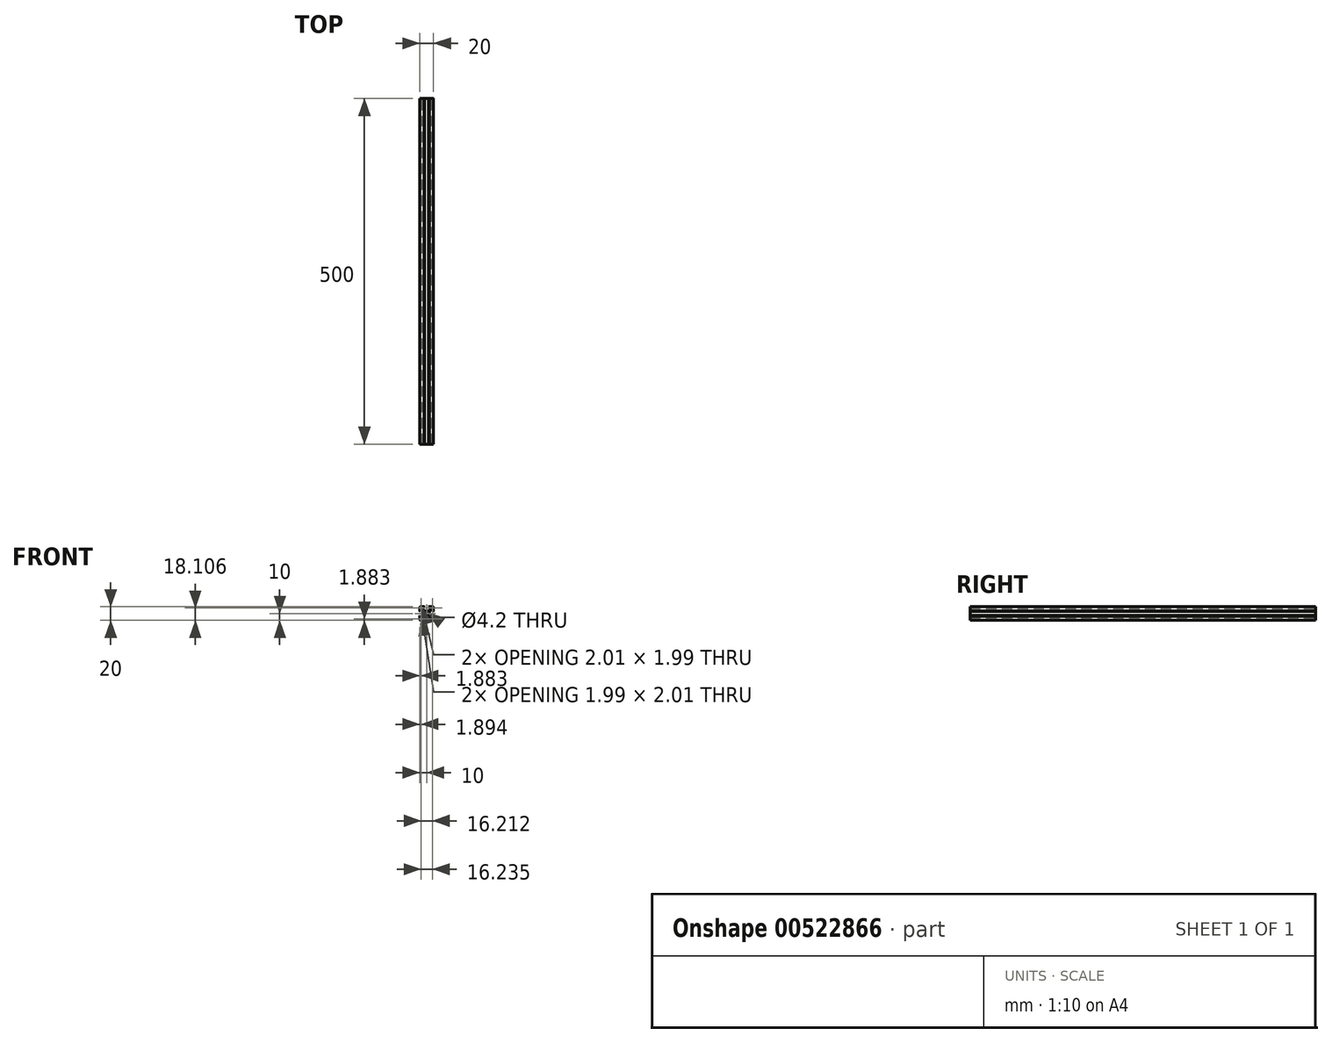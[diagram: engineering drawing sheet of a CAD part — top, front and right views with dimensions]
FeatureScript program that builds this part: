
annotation { "Feature Type Name" : "Feature", "Feature Type Description" : "" }
export const myFeature = defineFeature(function(context is Context, id is Id, definition is map)
    precondition{}
    {
        {
            var Q0;
            Q0=qCreatedBy(makeId("Front.planeOp"),FACE);
            var sketch = newSketch(context, id + "F0", { "sketchPlane" : qUnion([Q0])});
            skCircle(sketch, "E0", {"center": v(0, 0) * mm, "radius": 2.1 * mm});
            skLineSegment(sketch, "E1.bottom", {"start": v(-10, 10) * mm, "end": v(10, 10) * mm});
            skLineSegment(sketch, "E1.top", {"start": v(-10, -10) * mm, "end": v(10, -10) * mm});
            skLineSegment(sketch, "E1.left", {"start": v(-10, 10) * mm, "end": v(-10, -10) * mm});
            skLineSegment(sketch, "E1.right", {"start": v(10, 10) * mm, "end": v(10, -10) * mm});
            skLineSegment(sketch, "E2.bottom", {"start": v(-9.1, 9.1) * mm, "end": v(6.4, 9.1) * mm});
            skLineSegment(sketch, "E2.top", {"start": v(-9.1, -9.1) * mm, "end": v(9.1, -9.1) * mm});
            skLineSegment(sketch, "E2.left", {"start": v(-9.1, 9.1) * mm, "end": v(-9.1, -9.1) * mm});
            skLineSegment(sketch, "E2.right", {"start": v(9.1, 6.4) * mm, "end": v(9.1, -9.1) * mm});
            skLineSegment(sketch, "E3", {"start": v(-7.93, 7.93) * mm, "end": v(-1.48, 1.48) * mm});
            skLineSegment(sketch, "E4.0", {"start": v(7.46, 6.4) * mm, "end": v(1.92, 0.86) * mm});
            skLineSegment(sketch, "E5.MirrorCS", {"start": v(6.4, 7.46) * mm, "end": v(0.86, 1.92) * mm});
            skLineSegment(sketch, "E6.0", {"start": v(-8.47, 7.41) * mm, "end": v(-1.92, 0.86) * mm});
            skLineSegment(sketch, "E7.MirrorCS", {"start": v(-7.4, 8.46) * mm, "end": v(-0.86, 1.92) * mm});
            skPoint(sketch, "E8.orphan", {"position": v(-9.63, 8.57) * mm});
            skPoint(sketch, "E9.orphan", {"position": v(-8.57, 9.63) * mm});
            skPoint(sketch, "E10.orphan", {"position": v(8.05, 9.11) * mm});
            skPoint(sketch, "E11.orphan", {"position": v(9.11, 8.05) * mm});
            skPoint(sketch, "E12.orphan", {"position": v(9.63, -8.57) * mm});
            skPoint(sketch, "E13.orphan", {"position": v(8.57, -9.63) * mm});
            skPoint(sketch, "E14.orphan", {"position": v(-9.09, -10.15) * mm});
            skPoint(sketch, "E15.orphan", {"position": v(-10.15, -9.09) * mm});
            skLineSegment(sketch, "E16.trimOffspring", {"start": v(1.92, -0.86) * mm, "end": v(8.47, -7.41) * mm});
            skLineSegment(sketch, "E17.trimOffspring", {"start": v(0.86, -1.92) * mm, "end": v(7.4, -8.46) * mm});
            skLineSegment(sketch, "E18.trimOffspring", {"start": v(1.48, -1.48) * mm, "end": v(7.93, -7.93) * mm});
            skLineSegment(sketch, "E19.trimOffspring", {"start": v(-0.86, -1.92) * mm, "end": v(-7.41, -8.47) * mm});
            skLineSegment(sketch, "E20.trimOffspring", {"start": v(-1.48, -1.48) * mm, "end": v(-7.93, -7.93) * mm});
            skLineSegment(sketch, "E21.trimOffspring", {"start": v(-1.92, -0.86) * mm, "end": v(-8.46, -7.4) * mm});
            skLineSegment(sketch, "E22", {"start": v(-3.9, -2.84) * mm, "end": v(-3.9, 2.84) * mm});
            skLineSegment(sketch, "E23.1.0", {"start": v(2.84, -3.9) * mm, "end": v(-2.84, -3.9) * mm});
            skLineSegment(sketch, "E23.2.0", {"start": v(3.9, 2.84) * mm, "end": v(3.9, -2.84) * mm});
            skLineSegment(sketch, "E23.3.0", {"start": v(-2.84, 3.9) * mm, "end": v(2.84, 3.9) * mm});
            skLineSegment(sketch, "E24", {"start": v(-9.1, 2.84) * mm, "end": v(-9.1, -2.84) * mm});
            skLineSegment(sketch, "E25.1.0", {"start": v(-2.84, -9.1) * mm, "end": v(2.84, -9.1) * mm});
            skLineSegment(sketch, "E25.2.0", {"start": v(9.1, -2.84) * mm, "end": v(9.1, 2.84) * mm});
            skLineSegment(sketch, "E25.3.0", {"start": v(2.84, 9.1) * mm, "end": v(-2.84, 9.1) * mm});
            skLineSegment(sketch, "E26", {"start": v(-9.1, -2.84) * mm, "end": v(-10, -3.74) * mm});
            skLineSegment(sketch, "E27", {"start": v(-9.1, 2.84) * mm, "end": v(-10, 3.74) * mm});
            skLineSegment(sketch, "E28.1.0", {"start": v(-2.84, -9.1) * mm, "end": v(-3.74, -10) * mm});
            skLineSegment(sketch, "E28.1.1", {"start": v(2.84, -9.1) * mm, "end": v(3.74, -10) * mm});
            skLineSegment(sketch, "E28.2.0", {"start": v(9.1, -2.84) * mm, "end": v(10, -3.74) * mm});
            skLineSegment(sketch, "E28.2.1", {"start": v(9.1, 2.84) * mm, "end": v(10, 3.74) * mm});
            skLineSegment(sketch, "E28.3.0", {"start": v(2.84, 9.1) * mm, "end": v(3.74, 10) * mm});
            skLineSegment(sketch, "E28.3.1", {"start": v(-2.84, 9.1) * mm, "end": v(-3.74, 10) * mm});
            skLineSegment(sketch, "E29", {"start": v(-6.4, -9.1) * mm, "end": v(-6.4, -7.46) * mm});
            skLineSegment(sketch, "E30", {"start": v(-9.1, -6.4) * mm, "end": v(-7.46, -6.4) * mm});
            skLineSegment(sketch, "E31.1.0", {"start": v(6.4, -9.1) * mm, "end": v(6.4, -7.46) * mm});
            skLineSegment(sketch, "E31.1.1", {"start": v(9.1, -6.4) * mm, "end": v(7.46, -6.4) * mm});
            skLineSegment(sketch, "E31.2.0", {"start": v(9.1, 6.4) * mm, "end": v(7.46, 6.4) * mm});
            skLineSegment(sketch, "E31.2.1", {"start": v(6.4, 9.1) * mm, "end": v(6.4, 7.46) * mm});
            skLineSegment(sketch, "E31.3.0", {"start": v(-6.4, 9.1) * mm, "end": v(-6.4, 7.46) * mm});
            skLineSegment(sketch, "E31.3.1", {"start": v(-9.1, 6.4) * mm, "end": v(-7.46, 6.4) * mm});
            skPoint(sketch, "E32.start.orphan", {"position": v(9.1, 9.1) * mm});
            skLineSegment(sketch, "E33", {"start": v(7.47, 9.12) * mm, "end": v(9.1, 9.1) * mm});
            skLineSegment(sketch, "E34", {"start": v(9.1, 9.1) * mm, "end": v(9.1, 7.46) * mm});
            skLineSegment(sketch, "E35", {"start": v(7.47, 9.12) * mm, "end": v(7.11, 8.77) * mm});
            skLineSegment(sketch, "E36", {"start": v(9.1, 7.46) * mm, "end": v(8.74, 7.11) * mm});
            skLineSegment(sketch, "E37", {"start": v(8.74, 7.11) * mm, "end": v(7.11, 8.77) * mm});
            skLineSegment(sketch, "E38.1.0", {"start": v(-9.12, 7.47) * mm, "end": v(-8.77, 7.11) * mm});
            skLineSegment(sketch, "E38.1.1", {"start": v(-9.12, 7.47) * mm, "end": v(-9.1, 9.1) * mm});
            skLineSegment(sketch, "E38.1.2", {"start": v(-9.1, 9.1) * mm, "end": v(-7.46, 9.1) * mm});
            skLineSegment(sketch, "E38.1.3", {"start": v(-7.46, 9.1) * mm, "end": v(-7.11, 8.74) * mm});
            skLineSegment(sketch, "E38.1.4", {"start": v(-7.11, 8.74) * mm, "end": v(-8.77, 7.11) * mm});
            skLineSegment(sketch, "E38.2.0", {"start": v(-7.47, -9.12) * mm, "end": v(-7.11, -8.77) * mm});
            skLineSegment(sketch, "E38.2.1", {"start": v(-7.47, -9.12) * mm, "end": v(-9.1, -9.1) * mm});
            skLineSegment(sketch, "E38.2.2", {"start": v(-9.1, -9.1) * mm, "end": v(-9.1, -7.46) * mm});
            skLineSegment(sketch, "E38.2.3", {"start": v(-9.1, -7.46) * mm, "end": v(-8.74, -7.11) * mm});
            skLineSegment(sketch, "E38.2.4", {"start": v(-8.74, -7.11) * mm, "end": v(-7.11, -8.77) * mm});
            skLineSegment(sketch, "E38.3.0", {"start": v(9.12, -7.47) * mm, "end": v(8.77, -7.11) * mm});
            skLineSegment(sketch, "E38.3.1", {"start": v(9.12, -7.47) * mm, "end": v(9.1, -9.1) * mm});
            skLineSegment(sketch, "E38.3.2", {"start": v(9.1, -9.1) * mm, "end": v(7.46, -9.1) * mm});
            skLineSegment(sketch, "E38.3.3", {"start": v(7.46, -9.1) * mm, "end": v(7.11, -8.74) * mm});
            skLineSegment(sketch, "E38.3.4", {"start": v(7.11, -8.74) * mm, "end": v(8.77, -7.11) * mm});
            skSolve(sketch);
        }
        {
            var Q0;
            {var subQ5=sQuery(id+"F0.wireOp",EDGE,"E27");Q0=makeQuery(id+"F0.imprint","IMPRINT",FACE,{"disambiguationData":[TD([[makeQuery(id+"F0.imprint","IMPRINT",EDGE,{"derivedFrom":subQ5}),-1.0]])]});}
            var Q1;
            {var subQ0=sQuery(id+"F0.wireOp",EDGE,"E31.3.0");Q1=makeQuery(id+"F0.imprint","IMPRINT",FACE,{"disambiguationData":[TD([[makeQuery(id+"F0.imprint","IMPRINT",EDGE,{"derivedFrom":subQ0}),-1.0]])]});}
            var Q2;
            {var subQ0=sQuery(id+"F0.wireOp",EDGE,"E31.3.1");Q2=makeQuery(id+"F0.imprint","IMPRINT",FACE,{"disambiguationData":[TD([[makeQuery(id+"F0.imprint","IMPRINT",EDGE,{"derivedFrom":subQ0}),1.0]])]});}
            var Q3;
            {var subQ4=sQuery(id+"F0.wireOp",EDGE,"E3");Q3=makeQuery(id+"F0.imprint","IMPRINT",FACE,{"disambiguationData":[TD([[makeQuery(id+"F0.imprint","IMPRINT",EDGE,{"derivedFrom":subQ4}),-1.0]])]});}
            var Q4;
            {var subQ5=sQuery(id+"F0.wireOp",EDGE,"E3");Q4=makeQuery(id+"F0.imprint","IMPRINT",FACE,{"disambiguationData":[TD([[makeQuery(id+"F0.imprint","IMPRINT",EDGE,{"derivedFrom":subQ5}),1.0]])]});}
            var Q5;
            {var subQ0=sQuery(id+"F0.wireOp",EDGE,"E28.2.1");Q5=makeQuery(id+"F0.imprint","IMPRINT",FACE,{"disambiguationData":[TD([[makeQuery(id+"F0.imprint","IMPRINT",EDGE,{"derivedFrom":subQ0}),1.0]])]});}
            var Q6;
            {var subQ5=sQuery(id+"F0.wireOp",EDGE,"E23.2.0");Q6=makeQuery(id+"F0.imprint","IMPRINT",FACE,{"disambiguationData":[TD([[makeQuery(id+"F0.imprint","IMPRINT",EDGE,{"derivedFrom":subQ5}),-1.0]])]});}
            var Q7;
            {var subQ5=sQuery(id+"F0.wireOp",EDGE,"E23.3.0");Q7=makeQuery(id+"F0.imprint","IMPRINT",FACE,{"disambiguationData":[TD([[makeQuery(id+"F0.imprint","IMPRINT",EDGE,{"derivedFrom":subQ5}),-1.0]])]});}
            var Q8;
            {var subQ5=sQuery(id+"F0.wireOp",EDGE,"E22");Q8=makeQuery(id+"F0.imprint","IMPRINT",FACE,{"disambiguationData":[TD([[makeQuery(id+"F0.imprint","IMPRINT",EDGE,{"derivedFrom":subQ5}),-1.0]])]});}
            var Q9;
            {var subQ5=sQuery(id+"F0.wireOp",EDGE,"E23.1.0");Q9=makeQuery(id+"F0.imprint","IMPRINT",FACE,{"disambiguationData":[TD([[makeQuery(id+"F0.imprint","IMPRINT",EDGE,{"derivedFrom":subQ5}),-1.0]])]});}
            var Q10;
            {var subQ7=sQuery(id+"F0.wireOp",EDGE,"E20.trimOffspring");Q10=makeQuery(id+"F0.imprint","IMPRINT",FACE,{"disambiguationData":[TD([[makeQuery(id+"F0.imprint","IMPRINT",EDGE,{"derivedFrom":subQ7}),1.0]])]});}
            var Q11;
            {var subQ5=sQuery(id+"F0.wireOp",EDGE,"E20.trimOffspring");Q11=makeQuery(id+"F0.imprint","IMPRINT",FACE,{"disambiguationData":[TD([[makeQuery(id+"F0.imprint","IMPRINT",EDGE,{"derivedFrom":subQ5}),-1.0]])]});}
            var Q12;
            {var subQ7=sQuery(id+"F0.wireOp",EDGE,"E18.trimOffspring");Q12=makeQuery(id+"F0.imprint","IMPRINT",FACE,{"disambiguationData":[TD([[makeQuery(id+"F0.imprint","IMPRINT",EDGE,{"derivedFrom":subQ7}),-1.0]])]});}
            var Q13;
            {var subQ6=sQuery(id+"F0.wireOp",EDGE,"E18.trimOffspring");Q13=makeQuery(id+"F0.imprint","IMPRINT",FACE,{"disambiguationData":[TD([[makeQuery(id+"F0.imprint","IMPRINT",EDGE,{"derivedFrom":subQ6}),1.0]])]});}
            var Q14;
            {var subQ4=sQuery(id+"F0.wireOp",EDGE,"E28.1.1");Q14=makeQuery(id+"F0.imprint","IMPRINT",FACE,{"disambiguationData":[TD([[makeQuery(id+"F0.imprint","IMPRINT",EDGE,{"derivedFrom":subQ4}),1.0]])]});}
            var Q15;
            {var subQ0=sQuery(id+"F0.wireOp",EDGE,"E31.1.1");Q15=makeQuery(id+"F0.imprint","IMPRINT",FACE,{"disambiguationData":[TD([[makeQuery(id+"F0.imprint","IMPRINT",EDGE,{"derivedFrom":subQ0}),1.0]])]});}
            var Q16;
            {var subQ0=sQuery(id+"F0.wireOp",EDGE,"E31.1.0");Q16=makeQuery(id+"F0.imprint","IMPRINT",FACE,{"disambiguationData":[TD([[makeQuery(id+"F0.imprint","IMPRINT",EDGE,{"derivedFrom":subQ0}),-1.0]])]});}
            var Q17;
            {var subQ4=sQuery(id+"F0.wireOp",EDGE,"E26");Q17=makeQuery(id+"F0.imprint","IMPRINT",FACE,{"disambiguationData":[TD([[makeQuery(id+"F0.imprint","IMPRINT",EDGE,{"derivedFrom":subQ4}),1.0]])]});}
            var Q18;
            {var subQ7=sQuery(id+"F0.wireOp",EDGE,"E29");Q18=makeQuery(id+"F0.imprint","IMPRINT",FACE,{"disambiguationData":[TD([[makeQuery(id+"F0.imprint","IMPRINT",EDGE,{"derivedFrom":subQ7}),1.0]])]});}
            var Q19;
            {var subQ1=sQuery(id+"F0.wireOp",EDGE,"E30");Q19=makeQuery(id+"F0.imprint","IMPRINT",FACE,{"disambiguationData":[TD([[makeQuery(id+"F0.imprint","IMPRINT",EDGE,{"derivedFrom":subQ1}),-1.0]])]});}
            extrude(context, id + "F1", {"entities" : qUnion([Q0, Q1, Q2, Q3, Q4, Q5, Q6, Q7, Q8, Q9, Q10, Q11, Q12, Q13, Q14, Q15, Q16, Q17, Q18, Q19]), "depth" : 500 * mm, "offsetDistance" : 25 * mm});
        }
        {
            var Q0;
            Q0=makeQuery(id+"F1.opExtrude","SWEPT_EDGE",EDGE,{"disambiguationData":[OSD([sQuery(id+"F0.wireOp",EDGE,"E1.bottom"),sQuery(id+"F0.wireOp",EDGE,"E1.right")])]});
            var Q1;
            Q1=makeQuery(id+"F1.opExtrude","SWEPT_EDGE",EDGE,{"disambiguationData":[OSD([sQuery(id+"F0.wireOp",EDGE,"E1.bottom"),sQuery(id+"F0.wireOp",EDGE,"E1.left")])]});
            var Q2;
            Q2=makeQuery(id+"F1.opExtrude","SWEPT_EDGE",EDGE,{"disambiguationData":[OSD([sQuery(id+"F0.wireOp",EDGE,"E1.top"),sQuery(id+"F0.wireOp",EDGE,"E1.left")])]});
            var Q3;
            Q3=makeQuery(id+"F1.opExtrude","SWEPT_EDGE",EDGE,{"disambiguationData":[OSD([sQuery(id+"F0.wireOp",EDGE,"E1.top"),sQuery(id+"F0.wireOp",EDGE,"E1.right")])]});
            fillet(context, id + "F2", {"entities" : qUnion([Q0, Q1, Q2, Q3]), "radius" : 1.5 * mm, "tangentPropagation" : true, "allowEdgeOverflow" : false});
        }
    });
